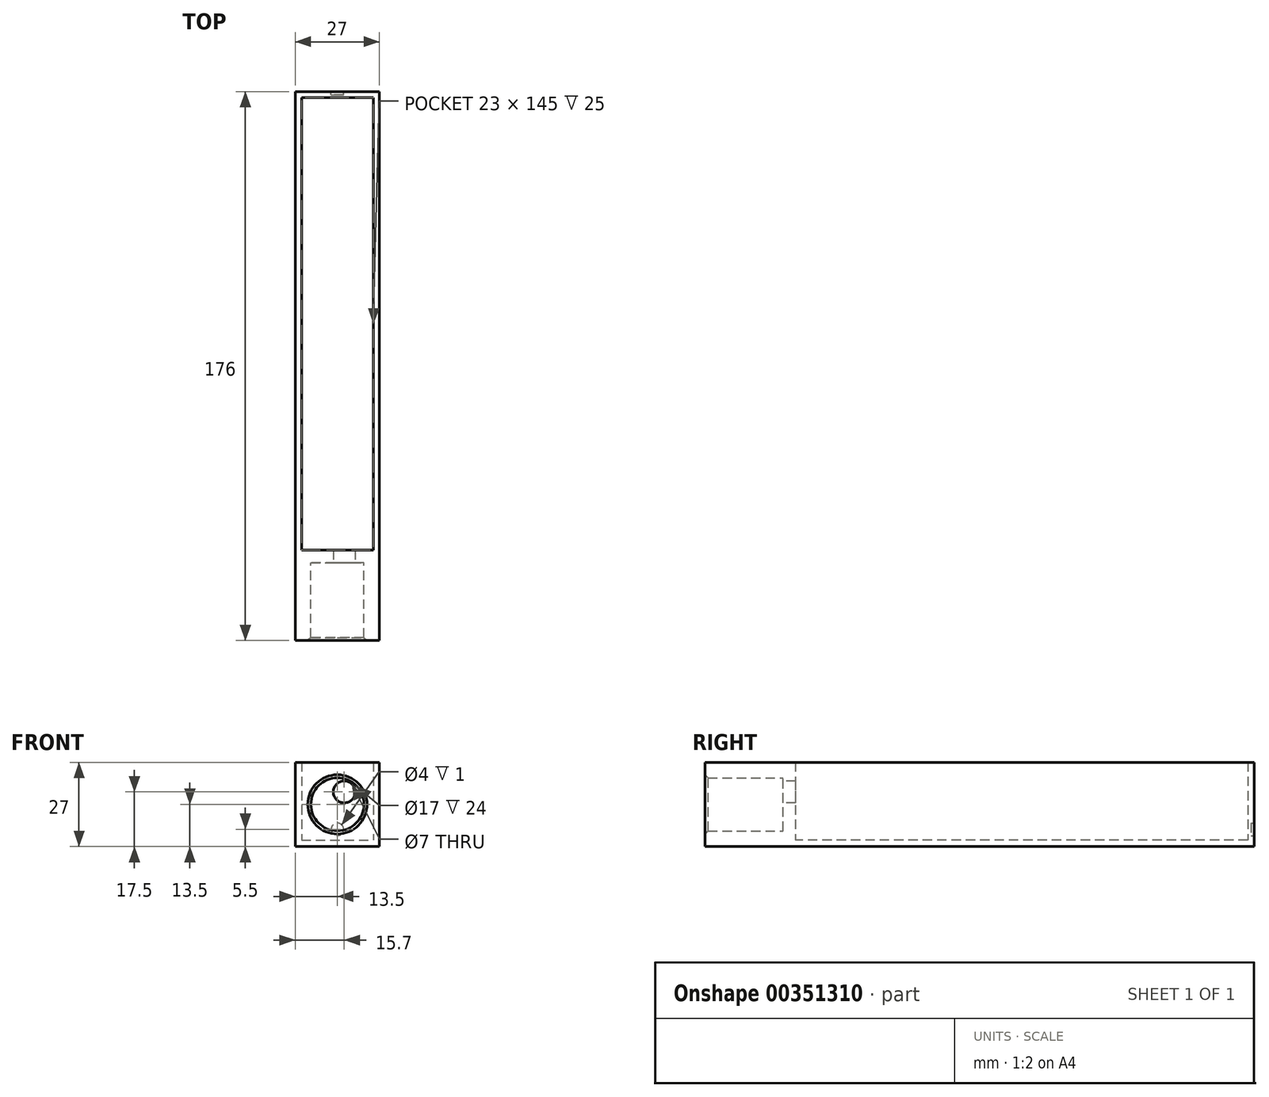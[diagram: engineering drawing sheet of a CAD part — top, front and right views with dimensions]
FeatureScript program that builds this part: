
annotation { "Feature Type Name" : "Feature", "Feature Type Description" : "" }
export const myFeature = defineFeature(function(context is Context, id is Id, definition is map)
    precondition{}
    {
        {
            var Q0;
            Q0=qCreatedBy(makeId("Top.planeOp"),FACE);
            var sketch = newSketch(context, id + "F0", { "sketchPlane" : qUnion([Q0])});
            skLineSegment(sketch, "E0.bottom", {"start": v(-11.5, 145) * mm, "end": v(11.5, 145) * mm});
            skLineSegment(sketch, "E0.top", {"start": v(-11.5, 0) * mm, "end": v(11.5, 0) * mm});
            skLineSegment(sketch, "E0.left", {"start": v(-11.5, 145) * mm, "end": v(-11.5, 0) * mm});
            skLineSegment(sketch, "E0.right", {"start": v(11.5, 145) * mm, "end": v(11.5, 0) * mm});
            skLineSegment(sketch, "E1.bottom", {"start": v(-13.5, 147) * mm, "end": v(13.5, 147) * mm});
            skLineSegment(sketch, "E1.top", {"start": v(-13.5, -4) * mm, "end": v(13.5, -4) * mm});
            skLineSegment(sketch, "E1.left", {"start": v(-13.5, 147) * mm, "end": v(-13.5, -4) * mm});
            skLineSegment(sketch, "E1.right", {"start": v(13.5, 147) * mm, "end": v(13.5, -4) * mm});
            skSolve(sketch);
        }
        {
            var Q0;
            Q0=makeQuery(id+"F0.imprint","IMPRINT",FACE,{"disambiguationData":[TD([[makeQuery(id+"F0.imprint","IMPRINT",EDGE,{"derivedFrom":sQuery(id+"F0.wireOp",EDGE,"E1.bottom")}),-1.0]])]});
            extrude(context, id + "F1", {"entities" : qUnion([Q0]), "depth" : 27 * mm});
        }
        {
            var Q0;
            Q0=makeQuery(id+"F1.opExtrude","SWEPT_FACE",FACE,{"disambiguationData":[OSD([sQuery(id+"F0.wireOp",EDGE,"E1.bottom")])]});
            var sketch = newSketch(context, id + "F2", { "sketchPlane" : qUnion([Q0])});
            skCircle(sketch, "E2", {"center": v(0, 5.5) * mm, "radius": 2 * mm});
            skPoint(sketch, "E2.centerSnap0", {"position": v(0, 0) * mm});
            skSolve(sketch);
        }
        {
            var Q0;
            Q0=makeQuery(id+"F0.imprint","IMPRINT",FACE,{"disambiguationData":[TD([[makeQuery(id+"F0.imprint","IMPRINT",EDGE,{"derivedFrom":sQuery(id+"F0.wireOp",EDGE,"E0.bottom")}),-1.0]])]});
            extrude(context, id + "F3", {"entities" : qUnion([Q0]), "operationType" : NewBodyOperationType.ADD, "depth" : 2 * mm});
        }
        {
            var Q0;
            Q0=makeQuery(id+"F2.imprint","IMPRINT",FACE,{"disambiguationData":[TD([[makeQuery(id+"F2.imprint","IMPRINT",EDGE,{"derivedFrom":sQuery(id+"F2.wireOp",EDGE,"E2")}),1.0]])]});
            extrude(context, id + "F4", {"entities" : qUnion([Q0]), "operationType" : NewBodyOperationType.REMOVE, "oppositeDirection" : true, "depth" : 1 * mm});
        }
        {
            var Q0;
            Q0=makeQuery(id+"F1.opExtrude","SWEPT_FACE",FACE,{"disambiguationData":[OSD([sQuery(id+"F0.wireOp",EDGE,"E1.top")])]});
            var sketch = newSketch(context, id + "F5", { "sketchPlane" : qUnion([Q0])});
            skCircle(sketch, "E3", {"center": v(0, 13.5) * mm, "radius": 8.5 * mm});
            skCircle(sketch, "E4", {"center": v(2.2, 17.5) * mm, "radius": 3.5 * mm});
            skSolve(sketch);
        }
        {
            var Q0;
            Q0=makeQuery(id+"F5.imprint","IMPRINT",FACE,{"disambiguationData":[TD([[makeQuery(id+"F5.imprint","IMPRINT",EDGE,{"derivedFrom":sQuery(id+"F5.wireOp",EDGE,"E3")}),-1.0]])]});
            extrude(context, id + "F6", {"entities" : qUnion([Q0]), "operationType" : NewBodyOperationType.ADD, "depth" : 25 * mm});
        }
        {
            var Q0;
            Q0=makeQuery(id+"F5.imprint","IMPRINT",FACE,{"disambiguationData":[TD([[makeQuery(id+"F5.imprint","IMPRINT",EDGE,{"derivedFrom":sQuery(id+"F5.wireOp",EDGE,"E4")}),1.0]])]});
            extrude(context, id + "F7", {"entities" : qUnion([Q0]), "operationType" : NewBodyOperationType.REMOVE, "endBound" : BoundingType.UP_TO_NEXT, "oppositeDirection" : true, "depth" : 25 * mm});
        }
        {
            var Q0;
            Q0=makeQuery(id+"F6.opExtrude","CAP_EDGE",EDGE,{"disambiguationData":[OSD([sQuery(id+"F5.wireOp",EDGE,"E3")])],"isStart":false});
            chamfer(context, id + "F8", {"entities" : qUnion([Q0]), "width" : 1 * mm, "tangentPropagation" : true});
        }
    });
